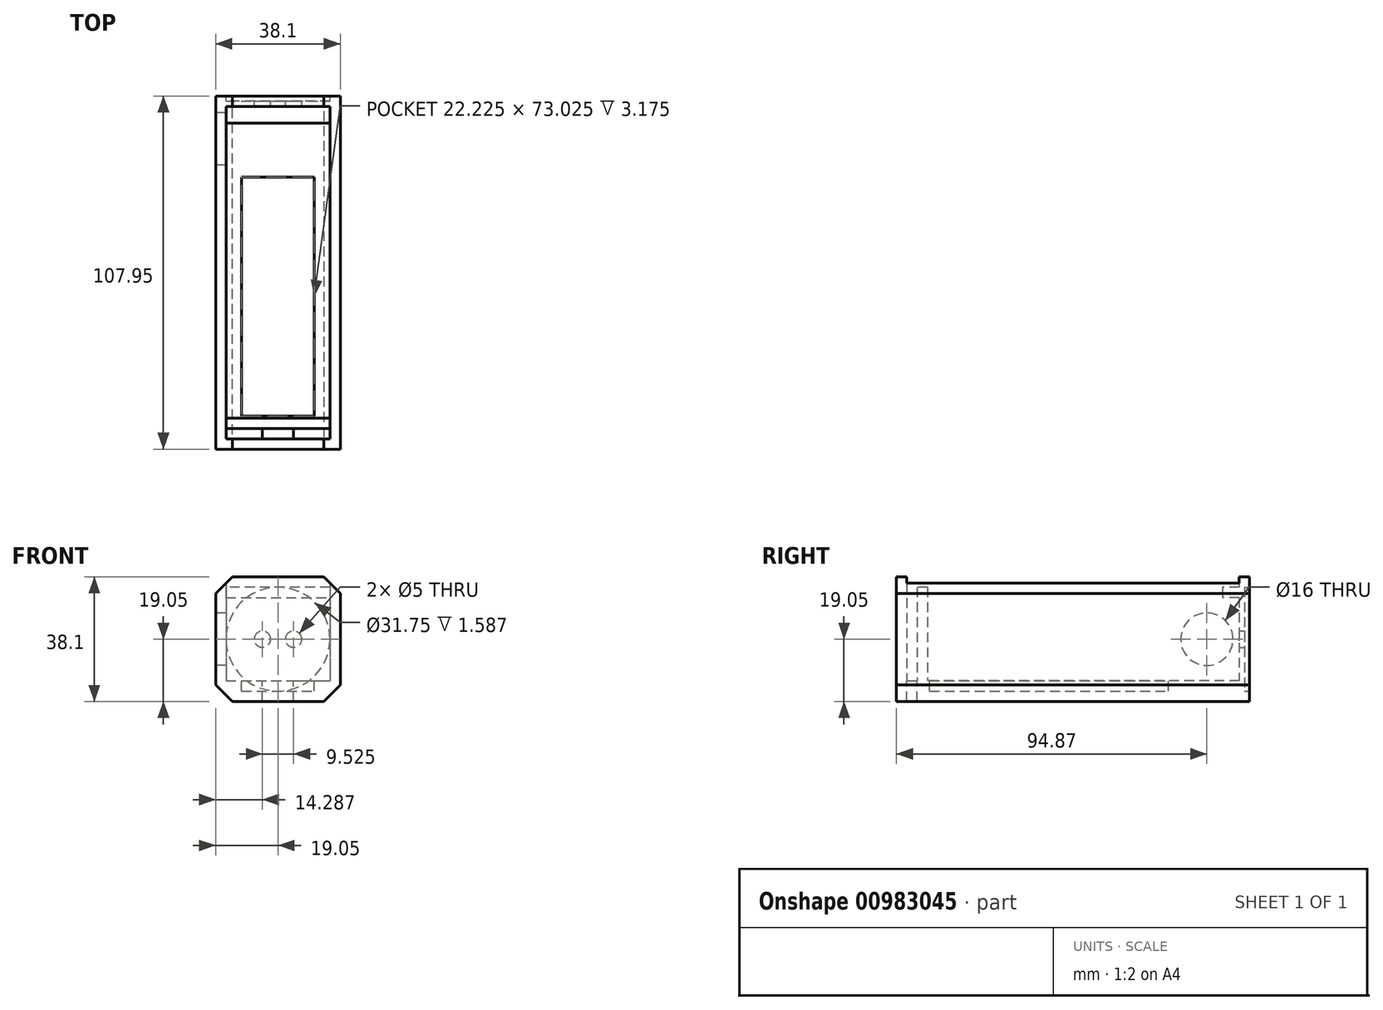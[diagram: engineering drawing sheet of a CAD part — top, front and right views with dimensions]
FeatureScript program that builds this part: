
annotation { "Feature Type Name" : "Feature", "Feature Type Description" : "" }
export const myFeature = defineFeature(function(context is Context, id is Id, definition is map)
    precondition{}
    {
        {
            var Q0;
            Q0=qCreatedBy(makeId("Top.planeOp"),FACE);
            var sketch = newSketch(context, id + "F0", { "sketchPlane" : qUnion([Q0])});
            skLineSegment(sketch, "E0.bottom", {"start": v(0, 0) * mm, "end": v(38.1, 0) * mm});
            skLineSegment(sketch, "E0.top", {"start": v(0, -107.95) * mm, "end": v(38.1, -107.95) * mm});
            skLineSegment(sketch, "E0.left", {"start": v(0, 0) * mm, "end": v(0, -107.95) * mm});
            skLineSegment(sketch, "E0.right", {"start": v(38.1, 0) * mm, "end": v(38.1, -107.95) * mm});
            skSolve(sketch);
        }
        {
            var Q0;
            Q0 = qSketchRegion(id + "F0", true);
            extrude(context, id + "F1", {"entities" : qUnion([Q0]), "depth" : 6.35 * mm, "offsetDistance" : 25.4 * mm});
        }
        {
            var Q0;
            Q0=makeQuery(id+"F1.opExtrude","CAP_FACE",FACE,{"disambiguationData":[OSD([sQuery(id+"F0.wireOp",EDGE,"E0.bottom"),sQuery(id+"F0.wireOp",EDGE,"E0.top"),sQuery(id+"F0.wireOp",EDGE,"E0.left"),sQuery(id+"F0.wireOp",EDGE,"E0.right")])],"isStart":false});
            var sketch = newSketch(context, id + "F2", { "sketchPlane" : qUnion([Q0])});
            skLineSegment(sketch, "E1.bottom", {"start": v(7.94, -97.8) * mm, "end": v(30.16, -97.8) * mm});
            skLineSegment(sketch, "E1.top", {"start": v(7.94, -24.76) * mm, "end": v(30.16, -24.76) * mm});
            skLineSegment(sketch, "E1.left", {"start": v(7.94, -97.8) * mm, "end": v(7.94, -24.76) * mm});
            skLineSegment(sketch, "E1.right", {"start": v(30.16, -97.8) * mm, "end": v(30.16, -24.76) * mm});
            skPoint(sketch, "E2", {"position": v(19.05, -97.8) * mm});
            skSolve(sketch);
        }
        {
            var Q0;
            Q0 = qSketchRegion(id + "F2", true);
            extrude(context, id + "F3", {"entities" : qUnion([Q0]), "operationType" : NewBodyOperationType.REMOVE, "oppositeDirection" : true, "depth" : 3.17 * mm, "offsetDistance" : 25.4 * mm});
        }
        {
            var Q0;
            Q0=makeQuery(id+"F1.opExtrude","CAP_FACE",FACE,{"disambiguationData":[OSD([sQuery(id+"F0.wireOp",EDGE,"E0.bottom"),sQuery(id+"F0.wireOp",EDGE,"E0.top"),sQuery(id+"F0.wireOp",EDGE,"E0.left"),sQuery(id+"F0.wireOp",EDGE,"E0.right")])],"isStart":false});
            var sketch = newSketch(context, id + "F4", { "sketchPlane" : qUnion([Q0])});
            skLineSegment(sketch, "E3", {"start": v(0, 0) * mm, "end": v(38.1, 0) * mm});
            skLineSegment(sketch, "E4", {"start": v(38.1, 0) * mm, "end": v(38.1, -107.95) * mm});
            skLineSegment(sketch, "E5", {"start": v(38.1, -107.95) * mm, "end": v(0, -107.95) * mm});
            skLineSegment(sketch, "E6", {"start": v(0, -107.95) * mm, "end": v(0, 0) * mm});
            skLineSegment(sketch, "E7", {"start": v(3.18, -3.18) * mm, "end": v(34.93, -3.17) * mm});
            skLineSegment(sketch, "E8", {"start": v(34.93, -3.17) * mm, "end": v(34.93, -104.78) * mm});
            skLineSegment(sketch, "E9", {"start": v(34.93, -104.78) * mm, "end": v(3.18, -104.78) * mm});
            skLineSegment(sketch, "E10", {"start": v(3.18, -104.78) * mm, "end": v(3.18, -3.17) * mm});
            skLineSegment(sketch, "E11", {"start": v(3.18, -101.6) * mm, "end": v(34.93, -101.6) * mm});
            skLineSegment(sketch, "E12", {"start": v(34.93, -101.6) * mm, "end": v(34.93, -98.43) * mm});
            skLineSegment(sketch, "E13", {"start": v(34.93, -98.43) * mm, "end": v(3.18, -98.43) * mm});
            skLineSegment(sketch, "E14", {"start": v(3.17, -98.43) * mm, "end": v(3.18, -101.6) * mm});
            skSolve(sketch);
        }
        {
            var Q0;
            Q0 = qSketchRegion(id + "F4", true);
            var Q1;
            Q1=makeQuery(id+"F4.imprint","IMPRINT",FACE,{"disambiguationData":[TD([[makeQuery(id+"F4.imprint","IMPRINT",EDGE,{"derivedFrom":sQuery(id+"F4.wireOp",EDGE,"E11")}),1.0]])]});
            extrude(context, id + "F5", {"entities" : qUnion([Q0, Q1]), "operationType" : NewBodyOperationType.ADD, "depth" : 31.75 * mm, "offsetDistance" : 25.4 * mm});
        }
        {
            var Q0;
            Q0=makeQuery(id+"F5.boolean.opBoolean","MERGE",FACE,{"derivedFrom":[makeQuery(id+"F1.opExtrude","SWEPT_FACE",FACE,{"disambiguationData":[OSD([sQuery(id+"F0.wireOp",EDGE,"E0.bottom")])]}),makeQuery(id+"F5.opExtrude","SWEPT_FACE",FACE,{"disambiguationData":[OSD([sQuery(id+"F4.wireOp",EDGE,"E3")])]})]});
            var sketch = newSketch(context, id + "F6", { "sketchPlane" : qUnion([Q0])});
            skCircle(sketch, "E15", {"center": v(-19.05, 19.05) * mm, "radius": 15.88 * mm});
            skPoint(sketch, "E15.centerSnap0", {"position": v(-38.1, 19.05) * mm});
            skPoint(sketch, "E15.centerSnap1", {"position": v(-19.05, 0) * mm});
            skCircle(sketch, "E16", {"center": v(-14.29, 19.05) * mm, "radius": 2.5 * mm});
            skCircle(sketch, "E17", {"center": v(-23.81, 19.05) * mm, "radius": 2.5 * mm});
            skSolve(sketch);
        }
        {
            var Q0;
            Q0 = qSketchRegion(id + "F6", true);
            extrude(context, id + "F7", {"entities" : qUnion([Q0]), "operationType" : NewBodyOperationType.REMOVE, "oppositeDirection" : true, "depth" : 1.59 * mm, "offsetDistance" : 25.4 * mm});
        }
        {
            var Q0;
            Q0=makeQuery(id+"F7.boolean.opBoolean","SPLIT",FACE,{"disambiguationData":[TD([makeQuery(id+"F7.opExtrude","SWEPT_FACE",FACE,{"disambiguationData":[OSD([sQuery(id+"F6.wireOp",EDGE,"E16")])]})])],"derivedFrom":makeQuery(id+"F5.boolean.opBoolean","MERGE",FACE,{"derivedFrom":[makeQuery(id+"F1.opExtrude","SWEPT_FACE",FACE,{"disambiguationData":[OSD([sQuery(id+"F0.wireOp",EDGE,"E0.bottom")])]}),makeQuery(id+"F5.opExtrude","SWEPT_FACE",FACE,{"disambiguationData":[OSD([sQuery(id+"F4.wireOp",EDGE,"E3")])]})]})});
            var sketch = newSketch(context, id + "F8", { "sketchPlane" : qUnion([Q0])});
            skCircle(sketch, "E18", {"center": v(-14.29, 19.05) * mm, "radius": 2.5 * mm});
            skCircle(sketch, "E19.0.0", {"center": v(-23.81, 19.05) * mm, "radius": 2.5 * mm});
            skSolve(sketch);
        }
        {
            var Q0;
            Q0 = qSketchRegion(id + "F8", true);
            extrude(context, id + "F9", {"entities" : qUnion([Q0]), "operationType" : NewBodyOperationType.REMOVE, "oppositeDirection" : true, "depth" : 25.4 * mm, "offsetDistance" : 25.4 * mm});
        }
        {
            var Q0;
            Q0=makeQuery(id+"F5.boolean.opBoolean","MERGE",FACE,{"derivedFrom":[makeQuery(id+"F1.opExtrude","SWEPT_FACE",FACE,{"disambiguationData":[OSD([sQuery(id+"F0.wireOp",EDGE,"E0.left")])]}),makeQuery(id+"F5.opExtrude","SWEPT_FACE",FACE,{"disambiguationData":[OSD([sQuery(id+"F4.wireOp",EDGE,"E6")])]})]});
            var sketch = newSketch(context, id + "F10", { "sketchPlane" : qUnion([Q0])});
            skCircle(sketch, "E20", {"center": v(13.08, 19.05) * mm, "radius": 8 * mm});
            skPoint(sketch, "E20.centerSnap0", {"position": v(0, 19.05) * mm});
            skSolve(sketch);
        }
        {
            var Q0;
            Q0 = qSketchRegion(id + "F10", true);
            extrude(context, id + "F11", {"entities" : qUnion([Q0]), "operationType" : NewBodyOperationType.REMOVE, "oppositeDirection" : true, "depth" : 25.4 * mm, "offsetDistance" : 25.4 * mm});
        }
        {
            var Q0;
            {var subQ0=sQuery(id+"F4.wireOp",EDGE,"E9");Q0=makeQuery(id+"F5.boolean.opBoolean","SPLIT",FACE,{"disambiguationData":[TD([makeQuery(id+"F5.opExtrude","SWEPT_FACE",FACE,{"disambiguationData":[OSD([subQ0])]})])],"derivedFrom":makeQuery(id+"F1.opExtrude","CAP_FACE",FACE,{"disambiguationData":[OSD([sQuery(id+"F0.wireOp",EDGE,"E0.bottom"),sQuery(id+"F0.wireOp",EDGE,"E0.top"),sQuery(id+"F0.wireOp",EDGE,"E0.left"),sQuery(id+"F0.wireOp",EDGE,"E0.right")])],"isStart":false})});}
            var sketch = newSketch(context, id + "F12", { "sketchPlane" : qUnion([Q0])});
            skLineSegment(sketch, "E21.bottom", {"start": v(14.29, -104.78) * mm, "end": v(23.81, -104.78) * mm});
            skLineSegment(sketch, "E21.top", {"start": v(14.29, -101.6) * mm, "end": v(23.81, -101.6) * mm});
            skLineSegment(sketch, "E21.left", {"start": v(14.29, -104.78) * mm, "end": v(14.29, -101.6) * mm});
            skLineSegment(sketch, "E21.right", {"start": v(23.81, -104.78) * mm, "end": v(23.81, -101.6) * mm});
            skLineSegment(sketch, "E22", {"start": v(3.18, -104.78) * mm, "end": v(14.29, -104.78) * mm});
            skLineSegment(sketch, "E23", {"start": v(23.81, -104.78) * mm, "end": v(34.93, -104.78) * mm});
            skSolve(sketch);
        }
        {
            var Q0;
            Q0 = qSketchRegion(id + "F12", true);
            extrude(context, id + "F13", {"entities" : qUnion([Q0]), "operationType" : NewBodyOperationType.REMOVE, "oppositeDirection" : true, "depth" : 25.4 * mm, "offsetDistance" : 25.4 * mm});
        }
        {
            var Q0;
            Q0=makeQuery(id+"F5.opExtrude","CAP_FACE",FACE,{"disambiguationData":[OSD([sQuery(id+"F4.wireOp",EDGE,"E3"),sQuery(id+"F4.wireOp",EDGE,"E4"),sQuery(id+"F4.wireOp",EDGE,"E5"),sQuery(id+"F4.wireOp",EDGE,"E6"),sQuery(id+"F4.wireOp",EDGE,"E7"),sQuery(id+"F4.wireOp",EDGE,"E8"),sQuery(id+"F4.wireOp",EDGE,"E9"),sQuery(id+"F4.wireOp",EDGE,"E10"),sQuery(id+"F4.wireOp",EDGE,"E11"),sQuery(id+"F4.wireOp",EDGE,"E13")])],"isStart":false});
            var sketch = newSketch(context, id + "F14", { "sketchPlane" : qUnion([Q0])});
            skLineSegment(sketch, "E24", {"start": v(3.18, -101.6) * mm, "end": v(3.18, -98.43) * mm});
            skLineSegment(sketch, "E25", {"start": v(3.18, -98.43) * mm, "end": v(34.93, -98.43) * mm});
            skLineSegment(sketch, "E26", {"start": v(34.93, -98.43) * mm, "end": v(34.93, -101.6) * mm});
            skLineSegment(sketch, "E27", {"start": v(34.93, -101.6) * mm, "end": v(3.18, -101.6) * mm});
            skSolve(sketch);
        }
        {
            var Q0;
            Q0 = qSketchRegion(id + "F14", true);
            extrude(context, id + "F15", {"entities" : qUnion([Q0]), "operationType" : NewBodyOperationType.REMOVE, "oppositeDirection" : true, "depth" : 3.17 * mm, "offsetDistance" : 25.4 * mm});
        }
        {
            var Q0;
            Q0=makeQuery(id+"F5.boolean.opBoolean","MERGE",FACE,{"derivedFrom":[makeQuery(id+"F1.opExtrude","SWEPT_FACE",FACE,{"disambiguationData":[OSD([sQuery(id+"F0.wireOp",EDGE,"E0.right")])]}),makeQuery(id+"F5.opExtrude","SWEPT_FACE",FACE,{"disambiguationData":[OSD([sQuery(id+"F4.wireOp",EDGE,"E4")])]})]});
            var sketch = newSketch(context, id + "F16", { "sketchPlane" : qUnion([Q0])});
            skLineSegment(sketch, "E28.bottom", {"start": v(-3.18, 34.93) * mm, "end": v(-8.26, 34.93) * mm});
            skLineSegment(sketch, "E28.top", {"start": v(-3.18, 31.75) * mm, "end": v(-8.26, 31.75) * mm});
            skLineSegment(sketch, "E28.left", {"start": v(-3.18, 34.93) * mm, "end": v(-3.18, 31.75) * mm});
            skLineSegment(sketch, "E28.right", {"start": v(-8.26, 34.93) * mm, "end": v(-8.26, 31.75) * mm});
            skSolve(sketch);
        }
        {
            var Q0;
            Q0 = qSketchRegion(id + "F16", true);
            extrude(context, id + "F17", {"entities" : qUnion([Q0]), "operationType" : NewBodyOperationType.ADD, "oppositeDirection" : true, "depth" : 38.1 * mm, "offsetDistance" : 25.4 * mm});
        }
        {
            var Q0;
            Q0=makeQuery(id+"F1.opExtrude","CAP_EDGE",EDGE,{"disambiguationData":[OSD([sQuery(id+"F0.wireOp",EDGE,"E0.right")])],"isStart":true});
            var Q1;
            Q1=makeQuery(id+"F5.opExtrude","CAP_EDGE",EDGE,{"disambiguationData":[OSD([sQuery(id+"F4.wireOp",EDGE,"E4")])],"isStart":false});
            var Q2;
            Q2=makeQuery(id+"F5.opExtrude","CAP_EDGE",EDGE,{"disambiguationData":[OSD([sQuery(id+"F4.wireOp",EDGE,"E6")])],"isStart":false});
            var Q3;
            Q3=makeQuery(id+"F1.opExtrude","CAP_EDGE",EDGE,{"disambiguationData":[OSD([sQuery(id+"F0.wireOp",EDGE,"E0.left")])],"isStart":true});
            chamfer(context, id + "F18", {"entities" : qUnion([Q0, Q1, Q2, Q3]), "width" : 5.08 * mm, "tangentPropagation" : true});
        }
    });
